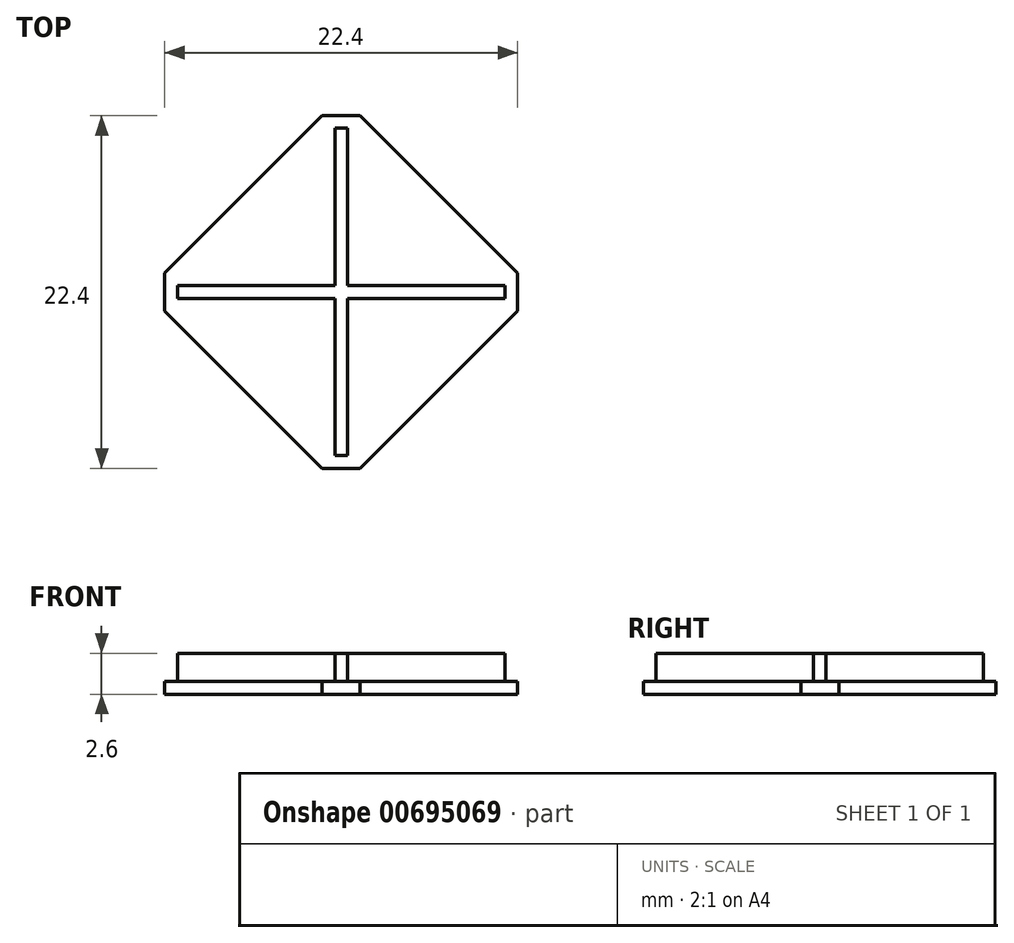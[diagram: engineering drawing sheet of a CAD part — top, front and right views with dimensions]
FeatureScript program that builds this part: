
annotation { "Feature Type Name" : "Feature", "Feature Type Description" : "" }
export const myFeature = defineFeature(function(context is Context, id is Id, definition is map)
    precondition{}
    {
        {
            var Q0;
            Q0=qCreatedBy(makeId("Top.planeOp"),FACE);
            var sketch = newSketch(context, id + "F0", { "sketchPlane" : qUnion([Q0])});
            skLineSegment(sketch, "E0", {"start": v(-0.4, 0.4) * mm, "end": v(-0.4, 10.4) * mm});
            skLineSegment(sketch, "E1", {"start": v(-0.4, 10.4) * mm, "end": v(0.4, 10.4) * mm});
            skLineSegment(sketch, "E2", {"start": v(0.4, 10.4) * mm, "end": v(0.4, 0.4) * mm});
            skLineSegment(sketch, "E3", {"start": v(0.4, 0.4) * mm, "end": v(10.4, 0.4) * mm});
            skLineSegment(sketch, "E4", {"start": v(10.4, 0.4) * mm, "end": v(10.4, -0.4) * mm});
            skLineSegment(sketch, "E5", {"start": v(10.4, -0.4) * mm, "end": v(0.4, -0.4) * mm});
            skLineSegment(sketch, "E6", {"start": v(0.4, -0.4) * mm, "end": v(0.4, -10.4) * mm});
            skLineSegment(sketch, "E7", {"start": v(0.4, -10.4) * mm, "end": v(-0.4, -10.4) * mm});
            skLineSegment(sketch, "E8", {"start": v(-0.4, -10.4) * mm, "end": v(-0.4, -0.4) * mm});
            skLineSegment(sketch, "E9", {"start": v(-0.4, -0.4) * mm, "end": v(-10.4, -0.4) * mm});
            skLineSegment(sketch, "E10", {"start": v(-10.4, -0.4) * mm, "end": v(-10.4, 0.4) * mm});
            skLineSegment(sketch, "E11", {"start": v(-10.4, 0.4) * mm, "end": v(-0.4, 0.4) * mm});
            skPoint(sketch, "E12", {"position": v(0, 10.4) * mm});
            skPoint(sketch, "E13", {"position": v(-10.4, 0) * mm});
            skLineSegment(sketch, "E14.0", {"start": v(-11.2, -1.2) * mm, "end": v(-11.2, 1.2) * mm});
            skLineSegment(sketch, "E14.1", {"start": v(1.2, 1.2) * mm, "end": v(11.2, 1.2) * mm});
            skLineSegment(sketch, "E14.2", {"start": v(1.2, 11.2) * mm, "end": v(1.2, 1.2) * mm});
            skLineSegment(sketch, "E14.3", {"start": v(-1.2, 11.2) * mm, "end": v(1.2, 11.2) * mm});
            skLineSegment(sketch, "E14.4", {"start": v(-1.2, 1.2) * mm, "end": v(-1.2, 11.2) * mm});
            skLineSegment(sketch, "E14.5", {"start": v(11.2, 1.2) * mm, "end": v(11.2, -1.2) * mm});
            skLineSegment(sketch, "E14.6", {"start": v(-11.2, 1.2) * mm, "end": v(-1.2, 1.2) * mm});
            skLineSegment(sketch, "E14.7", {"start": v(11.2, -1.2) * mm, "end": v(1.2, -1.2) * mm});
            skLineSegment(sketch, "E14.8", {"start": v(1.2, -1.2) * mm, "end": v(1.2, -11.2) * mm});
            skLineSegment(sketch, "E14.9", {"start": v(1.2, -11.2) * mm, "end": v(-1.2, -11.2) * mm});
            skLineSegment(sketch, "E14.10", {"start": v(-1.2, -11.2) * mm, "end": v(-1.2, -1.2) * mm});
            skLineSegment(sketch, "E14.11", {"start": v(-1.2, -1.2) * mm, "end": v(-11.2, -1.2) * mm});
            skLineSegment(sketch, "E15", {"start": v(-11.2, 1.2) * mm, "end": v(-1.2, 11.2) * mm});
            skLineSegment(sketch, "E16", {"start": v(1.2, 11.2) * mm, "end": v(11.2, 1.2) * mm});
            skLineSegment(sketch, "E17", {"start": v(11.2, -1.2) * mm, "end": v(1.2, -11.2) * mm});
            skLineSegment(sketch, "E18", {"start": v(-1.2, -11.2) * mm, "end": v(-11.2, -1.2) * mm});
            skSolve(sketch);
        }
        {
            var Q0;
            Q0=makeQuery(id+"F0.imprint","IMPRINT",FACE,{"disambiguationData":[TD([[makeQuery(id+"F0.imprint","IMPRINT",EDGE,{"derivedFrom":sQuery(id+"F0.wireOp",EDGE,"E0")}),-1.0]])]});
            extrude(context, id + "F1", {"entities" : qUnion([Q0]), "depth" : 1.8 * mm, "offsetDistance" : 25 * mm});
        }
        {
            var Q0;
            Q0=makeQuery(id+"F0.imprint","IMPRINT",FACE,{"disambiguationData":[TD([[makeQuery(id+"F0.imprint","IMPRINT",EDGE,{"derivedFrom":sQuery(id+"F0.wireOp",EDGE,"E14.4")}),1.0]])]});
            var Q1;
            Q1=makeQuery(id+"F0.imprint","IMPRINT",FACE,{"disambiguationData":[TD([[makeQuery(id+"F0.imprint","IMPRINT",EDGE,{"derivedFrom":sQuery(id+"F0.wireOp",EDGE,"E14.1")}),1.0]])]});
            var Q2;
            Q2=makeQuery(id+"F0.imprint","IMPRINT",FACE,{"disambiguationData":[TD([[makeQuery(id+"F0.imprint","IMPRINT",EDGE,{"derivedFrom":sQuery(id+"F0.wireOp",EDGE,"E14.7")}),1.0]])]});
            var Q3;
            Q3=makeQuery(id+"F0.imprint","IMPRINT",FACE,{"disambiguationData":[TD([[makeQuery(id+"F0.imprint","IMPRINT",EDGE,{"derivedFrom":sQuery(id+"F0.wireOp",EDGE,"E14.10")}),1.0]])]});
            var Q4;
            Q4=makeQuery(id+"F0.imprint","IMPRINT",FACE,{"disambiguationData":[TD([[makeQuery(id+"F0.imprint","IMPRINT",EDGE,{"derivedFrom":sQuery(id+"F0.wireOp",EDGE,"E0")}),1.0]])]});
            var Q5;
            Q5=makeQuery(id+"F1.opExtrude","CAP_FACE",FACE,{"disambiguationData":[OSD([sQuery(id+"F0.wireOp",EDGE,"E0"),sQuery(id+"F0.wireOp",EDGE,"E1"),sQuery(id+"F0.wireOp",EDGE,"E2"),sQuery(id+"F0.wireOp",EDGE,"E3"),sQuery(id+"F0.wireOp",EDGE,"E4"),sQuery(id+"F0.wireOp",EDGE,"E5"),sQuery(id+"F0.wireOp",EDGE,"E6"),sQuery(id+"F0.wireOp",EDGE,"E7"),sQuery(id+"F0.wireOp",EDGE,"E8"),sQuery(id+"F0.wireOp",EDGE,"E9"),sQuery(id+"F0.wireOp",EDGE,"E10"),sQuery(id+"F0.wireOp",EDGE,"E11")])],"isStart":false});
            var Q6;
            Q6=makeQuery(id+"F0.imprint","IMPRINT",FACE,{"disambiguationData":[TD([[makeQuery(id+"F0.imprint","IMPRINT",EDGE,{"derivedFrom":sQuery(id+"F0.wireOp",EDGE,"E0")}),-1.0]])]});
            extrude(context, id + "F2", {"entities" : qUnion([Q0, Q1, Q2, Q3, Q4, Q5, Q6]), "operationType" : NewBodyOperationType.ADD, "oppositeDirection" : true, "depth" : 0.8 * mm, "offsetDistance" : 25 * mm});
        }
    });
